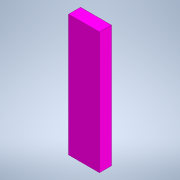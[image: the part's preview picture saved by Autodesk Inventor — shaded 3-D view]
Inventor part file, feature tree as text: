
AUTODESK INVENTOR PART (.ipt)
format: ipt  version: 2020 (Build 240168000, 168)  size: 92,160 bytes
history: native  units: in
note: dims shown in document units (in); Inventor stores cm internally (conversion verified against a paired STEP export)
features: extrude x1, sketch x1
ambient origin geometry x8: Origin, YZ Plane, XZ Plane, XY Plane, X Axis, Y Axis, Z Axis, Center Point
bodies: Solid1 (feature_tree)
feature tree (2):
  extrude  "Extrusion1"  Depth=0.7874in
  sketch  "Sketch1"  dims[d0=3.1102in d1=0.7874in d2=0.3051in d3=0.0in]
